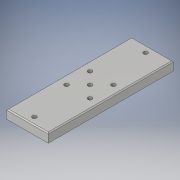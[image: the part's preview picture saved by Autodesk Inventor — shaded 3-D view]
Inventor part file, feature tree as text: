
AUTODESK INVENTOR PART (.ipt)
format: ipt  version: 2019.4 (Build 234330000, 330)  size: 159,232 bytes
history: native  units: in
note: dims shown in document units (in); Inventor stores cm internally (conversion verified against a paired STEP export)
features: sketch x5, extrude x4, hole x1, fillet x1, chamfer x1
ambient origin geometry x8: Origin, YZ Plane, XZ Plane, XY Plane, X Axis, Y Axis, Z Axis, Center Point
bodies: Solid1 (feature_tree)
feature tree (12):
  extrude  "Extrusion1"  Depth=1.181in
  hole  "Hole1"  [1 undecoded]
  extrude  "Extrusion2"  Depth=0.7874in
  extrude  "Extrusion3"  Depth=0.059in
  fillet  "Fillet1"  Radius=0.25in
  extrude  "Extrusion4"  Depth=0.315in
  chamfer  "Chamfer2"  Distance=2.756in
  sketch  "Sketch1"  dims[d0=3.543in d1=1.181in]
  sketch  "Sketch2"  dims[d2=0.25in d3=0.0in d4=0.118in]
  sketch  "Sketch3"  dims[d5=0.3315in d6=0.7874in d8=0.663in d9=0.7874in d11=0.663in]
  sketch  "Sketch4"  dims[d14=0.3315in]
  sketch  "Sketch5"  dims[d15=0.118in d16=0.18in d17=0.375in d18=0.25in d19=0.5635in d20=0.22in d21=0.8108in d22=0.118in d23=0.25in d24=0.0in d25=0.315in d26=2.756in d27=0.059in d28=0.0in d29=0.08in d33=0.118in d34=0.118in d35=0.197in d36=0.197in d37=0.059in d38=0.0in d39=0.028in d40=0.125in d41=45.0deg]
note: 1 required parameter value undecoded (feature->parameter linkage not recoverable at this tier; creation-order binding heuristic only, values carry confidence <= 0.55)
